# Revit family: Valve_Backwater-Zurn-Z1740
name_source: partatom
category: Plumbing Fixtures
units: mm (PartAtom-declared; Revit-internal decimal feet)

## family parameters
Always vertical = Yes
Cut with Voids When Loaded = No
Maintain Annotation Orientation = No
OmniClass Number = 23.65.55.14
OmniClass Title = Valves for Liquid Services
Part Type = Normal
Room Calculation Point = No
Round Connector Dimension = Use Radius
Shared = No
Work Plane-Based = No

## types (2) — shared parameters
Approx. Wt. Lbs = 40 "
Assembly Code = D2040100
CW Connection = No
Default Elevation = 25 "
Description = BACKWATER VALVE
Dimension A = 4 "
Dimension A1 = 2 "
Dimension B = 5 "
Dimension B1 = 2.5 "
Dimension E = 5.625 "
Dimension G = 8.5 "
Dimension J = 6.75 "
Dimension K = 4.125 "
HW Connection = No
Manufacturer = Zurn Water, LLC
Manufacturer Brand = Zurn
Modified Date = 12/19/2025
Pipe Size A (Actual Radius) = 2.25 "
Pipe Size A (Diameter) = 4 "
Pipe Size A (Inner Radius) = 2.013 "
Pipe Size A (Nominal Radius) = 2 "
Product Documentation Link = https://files.zurn.com
Product Page URL = https://www.zurn.com
Product data url = https://www.bimobject.com
URL = www.zurn.com
Valve Length = 15 "
Vent Connection = No
WFU = 1
Waste Connection = Yes
zero-valued in all types: CWFU, HWFU

## per-type parameters (varying)
| type | Main Material | Model |
| Z1740-4 Inch-Butt Weld Outlet | Steel - Zurn - Stainless - Type - 304 | Z1740 |
| ZM1740-4 Inch-Butt Weld Outlet | Steel - Zurn - Stainless - Type - 316 | ZM1740 |

## geometry (parser evidence)
native form markers: Blend x2, Sweep x4
no freeform markers — native parametric forms only
